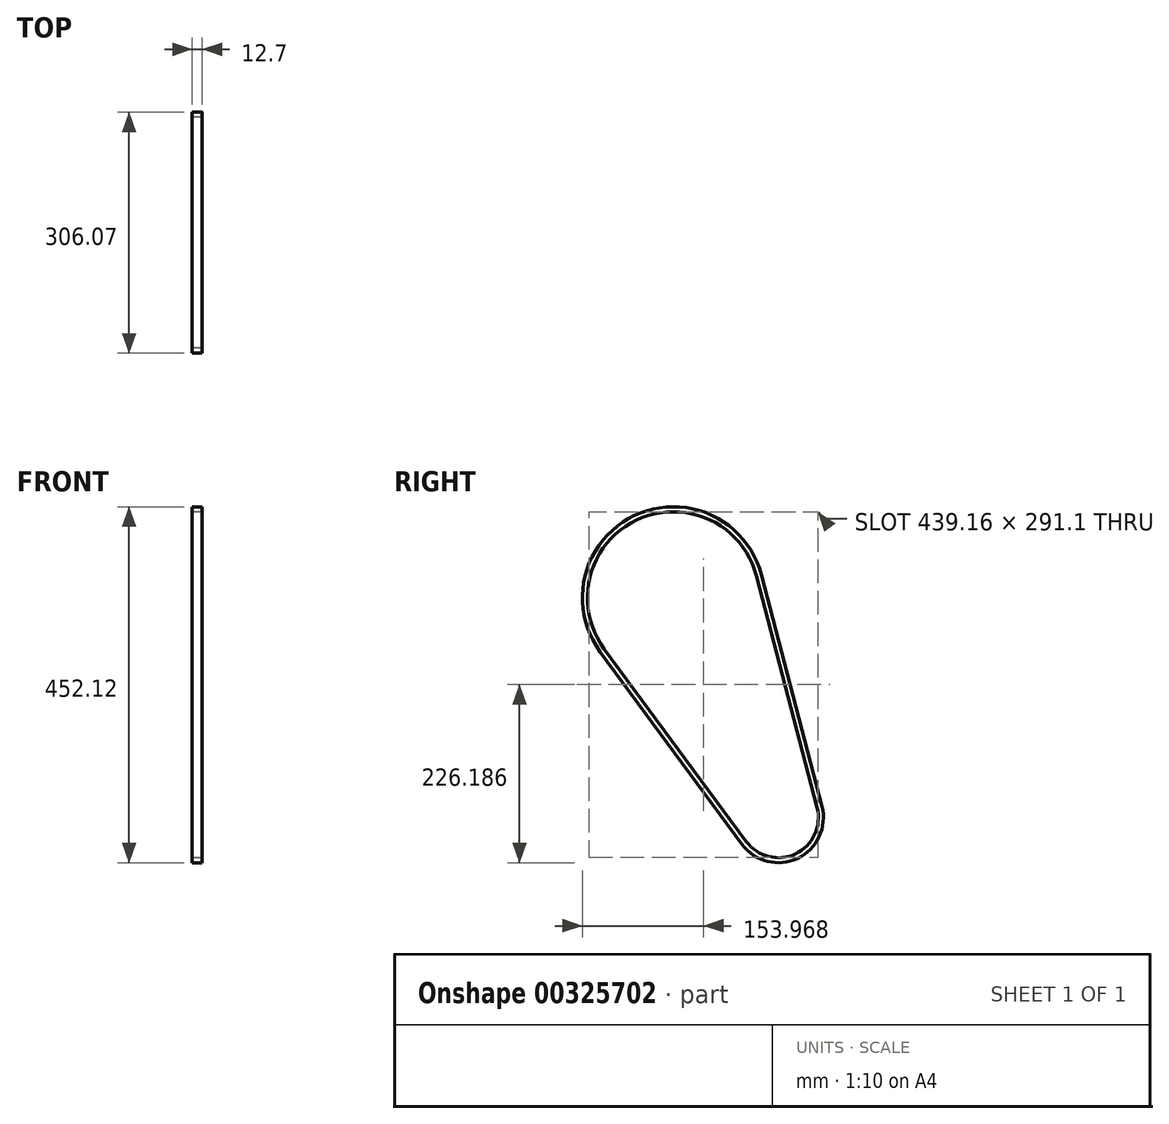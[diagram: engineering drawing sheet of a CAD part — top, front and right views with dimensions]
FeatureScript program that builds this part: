
annotation { "Feature Type Name" : "Feature", "Feature Type Description" : "" }
export const myFeature = defineFeature(function(context is Context, id is Id, definition is map)
    precondition{}
    {
        {
            var Q0;
            Q0=qCreatedBy(makeId("Right.planeOp"),FACE);
            var sketch = newSketch(context, id + "F0", { "sketchPlane" : qUnion([Q0])});
            skLineSegment(sketch, "E0", {"start": v(0, 0) * mm, "end": v(0, -279.4) * mm, "construction": true});
            skLineSegment(sketch, "E1", {"start": v(0, -279.4) * mm, "end": v(133.35, -279.4) * mm, "construction": true});
            skArc(sketch, "E2", {"start": v(105.68, 27.6) * mm, "mid": v(-47.04, 98.57) * mm, "end": v(-87.92, -64.8) * mm});
            skArc(sketch, "E3", {"start": v(92.46, -309.54) * mm, "mid": v(155.23, -325.25) * mm, "end": v(182.5, -266.56) * mm});
            skLineSegment(sketch, "E4", {"start": v(105.68, 27.6) * mm, "end": v(182.5, -266.56) * mm});
            skLineSegment(sketch, "E5", {"start": v(-87.92, -64.8) * mm, "end": v(92.46, -309.54) * mm});
            skLineSegment(sketch, "E6.0", {"start": v(111.82, 29.2) * mm, "end": v(188.65, -264.96) * mm});
            skArc(sketch, "E6.1", {"start": v(111.82, 29.2) * mm, "mid": v(-49.78, 104.3) * mm, "end": v(-93.03, -68.57) * mm});
            skLineSegment(sketch, "E6.2", {"start": v(-93.03, -68.57) * mm, "end": v(87.34, -313.3) * mm});
            skArc(sketch, "E6.3", {"start": v(87.34, -313.3) * mm, "mid": v(157.97, -330.98) * mm, "end": v(188.65, -264.96) * mm});
            skSolve(sketch);
        }
        {
            var Q0;
            Q0 = qSketchRegion(id + "F0", true);
            extrude(context, id + "F1", {"entities" : qUnion([Q0]), "endBound" : BoundingType.SYMMETRIC, "depth" : 12.7 * mm});
        }
    });
